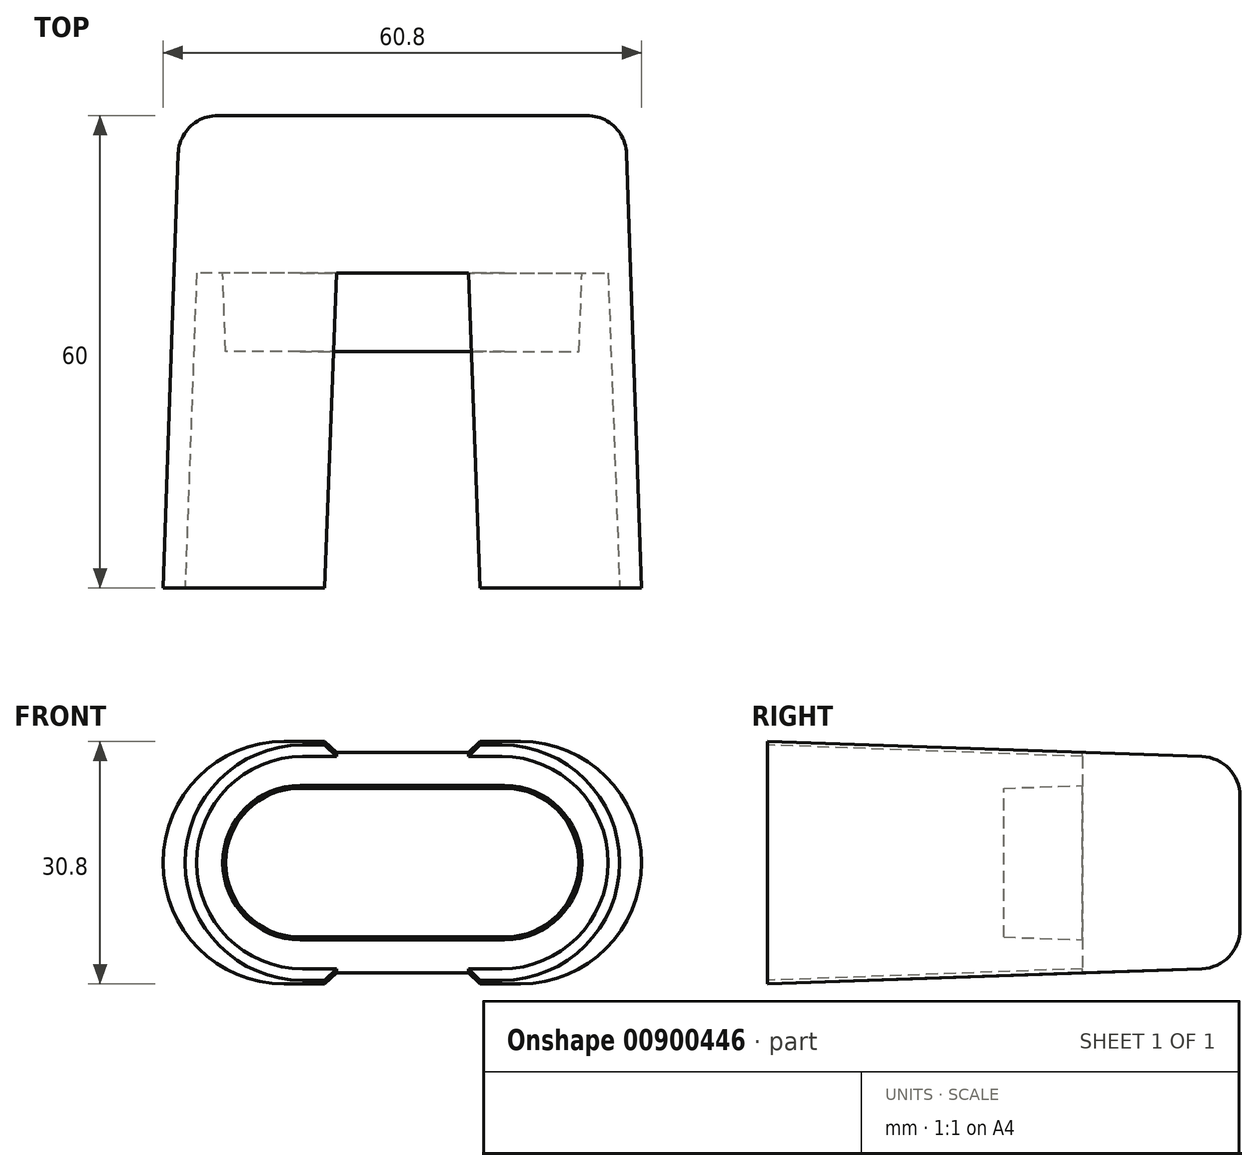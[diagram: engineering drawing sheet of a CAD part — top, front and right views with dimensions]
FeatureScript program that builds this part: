
annotation { "Feature Type Name" : "Feature", "Feature Type Description" : "" }
export const myFeature = defineFeature(function(context is Context, id is Id, definition is map)
    precondition{}
    {
        {
            var Q0;
            Q0=qCreatedBy(makeId("Front.planeOp"),FACE);
            var sketch = newSketch(context, id + "F0", { "sketchPlane" : qUnion([Q0])});
            skLineSegment(sketch, "E0", {"start": v(0, 0) * mm, "end": v(-28.3, 0) * mm, "construction": true});
            skLineSegment(sketch, "E1", {"start": v(0, 0) * mm, "end": v(0, 13.5) * mm, "construction": true});
            skLineSegment(sketch, "E2", {"start": v(-28.3, 0) * mm, "end": v(-28.3, 0) * mm});
            skLineSegment(sketch, "E3", {"start": v(-15, 13.3) * mm, "end": v(15, 13.3) * mm});
            skLineSegment(sketch, "E4", {"start": v(28.3, 0) * mm, "end": v(28.3, 0) * mm});
            skLineSegment(sketch, "E5", {"start": v(15, -13.3) * mm, "end": v(-15, -13.3) * mm});
            skPoint(sketch, "E6.visualSharp", {"position": v(-28.3, 13.3) * mm});
            skArc(sketch, "E6.filletArc", {"start": v(-15, 13.3) * mm, "mid": v(-24.4, 9.4) * mm, "end": v(-28.3, 0) * mm});
            skPoint(sketch, "E7.visualSharp", {"position": v(-28.3, -13.3) * mm});
            skArc(sketch, "E7.filletArc", {"start": v(-28.3, 0) * mm, "mid": v(-24.4, -9.4) * mm, "end": v(-15, -13.3) * mm});
            skPoint(sketch, "E8.visualSharp", {"position": v(28.3, -13.3) * mm});
            skArc(sketch, "E8.filletArc", {"start": v(15, -13.3) * mm, "mid": v(24.4, -9.4) * mm, "end": v(28.3, 0) * mm});
            skPoint(sketch, "E9.visualSharp", {"position": v(28.3, 13.3) * mm});
            skArc(sketch, "E9.filletArc", {"start": v(28.3, 0) * mm, "mid": v(24.4, 9.4) * mm, "end": v(15, 13.3) * mm});
            skSolve(sketch);
        }
        {
            var Q0;
            Q0=makeQuery(id+"F0.imprint","IMPRINT",FACE,{"disambiguationData":[TD([[makeQuery(id+"F0.imprint","IMPRINT",EDGE,{"derivedFrom":sQuery(id+"F0.wireOp",EDGE,"E3")}),-1.0]])]});
            extrude(context, id + "F1", {"entities" : qUnion([Q0]), "depth" : 60 * mm, "offsetDistance" : 25 * mm, "hasDraft" : true, "draftAngle" : 2 * degree});
        }
        {
            var Q0;
            Q0=qCreatedBy(makeId("Front.planeOp"),FACE);
            var sketch = newSketch(context, id + "F2", { "sketchPlane" : qUnion([Q0])});
            skLineSegment(sketch, "E10", {"start": v(0, 0) * mm, "end": v(-25.4, 0) * mm, "construction": true});
            skLineSegment(sketch, "E11", {"start": v(-25.4, 0) * mm, "end": v(-25.4, 0) * mm});
            skLineSegment(sketch, "E12", {"start": v(25.4, 0) * mm, "end": v(25.4, 0) * mm});
            skPoint(sketch, "E13.visualSharp", {"position": v(-25.4, 12.75) * mm});
            skArc(sketch, "E13.filletArc", {"start": v(-12.65, 12.75) * mm, "mid": v(-21.67, 9.02) * mm, "end": v(-25.4, 0) * mm});
            skPoint(sketch, "E14.visualSharp", {"position": v(-25.4, -12.75) * mm});
            skArc(sketch, "E14.filletArc", {"start": v(-25.4, 0) * mm, "mid": v(-21.67, -9.02) * mm, "end": v(-12.65, -12.75) * mm});
            skPoint(sketch, "E15.visualSharp", {"position": v(25.4, -12.75) * mm});
            skArc(sketch, "E15.filletArc", {"start": v(12.65, -12.75) * mm, "mid": v(21.67, -9.02) * mm, "end": v(25.4, 0) * mm});
            skPoint(sketch, "E16.visualSharp", {"position": v(25.4, 12.75) * mm});
            skArc(sketch, "E16.filletArc", {"start": v(25.4, 0) * mm, "mid": v(21.67, 9.02) * mm, "end": v(12.65, 12.75) * mm});
            skLineSegment(sketch, "E17", {"start": v(12.65, 12.75) * mm, "end": v(7.65, 12.75) * mm});
            skLineSegment(sketch, "E18", {"start": v(-12.65, 12.75) * mm, "end": v(-7.65, 12.75) * mm});
            skLineSegment(sketch, "E19", {"start": v(12.65, -12.75) * mm, "end": v(7.65, -12.75) * mm});
            skLineSegment(sketch, "E20", {"start": v(-12.65, -12.75) * mm, "end": v(-7.65, -12.75) * mm});
            skLineSegment(sketch, "E21", {"start": v(7.65, 12.75) * mm, "end": v(7.65, 18.8) * mm});
            skLineSegment(sketch, "E22", {"start": v(7.65, 18.8) * mm, "end": v(-7.65, 18.8) * mm});
            skLineSegment(sketch, "E23", {"start": v(-7.65, 12.75) * mm, "end": v(-7.65, 18.8) * mm});
            skLineSegment(sketch, "E24", {"start": v(7.65, -12.75) * mm, "end": v(7.65, -18.81) * mm});
            skLineSegment(sketch, "E25", {"start": v(7.65, -18.81) * mm, "end": v(-7.65, -18.81) * mm});
            skLineSegment(sketch, "E26", {"start": v(-7.65, -18.81) * mm, "end": v(-7.65, -12.75) * mm});
            skSolve(sketch);
        }
        {
            var Q0;
            Q0 = qSketchRegion(id + "F2", true);
            extrude(context, id + "F3", {"entities" : qUnion([Q0]), "operationType" : NewBodyOperationType.REMOVE, "depth" : 60 * mm, "offsetDistance" : 25 * mm, "hasDraft" : true, "draftAngle" : 2.1 * degree, "hasSecondDirection" : true, "secondDirectionOppositeDirection" : false, "secondDirectionDepth" : 20 * mm});
        }
        {
            var Q0;
            Q0=makeQuery(id+"F1.opExtrude","CAP_EDGE",EDGE,{"disambiguationData":[OSD([sQuery(id+"F0.wireOp",EDGE,"E6.filletArc"),sQuery(id+"F0.wireOp",EDGE,"E7.filletArc")])],"isStart":true});
            fillet(context, id + "F4", {"entities" : qUnion([Q0]), "radius" : 5 * mm, "tangentPropagation" : true, "allowEdgeOverflow" : false});
        }
        {
            var Q0;
            Q0=qCreatedBy(makeId("Front.planeOp"),FACE);
            var sketch = newSketch(context, id + "F5", { "sketchPlane" : qUnion([Q0])});
            skLineSegment(sketch, "E27", {"start": v(0, 0) * mm, "end": v(23.5, 0) * mm, "construction": true});
            skLineSegment(sketch, "E28", {"start": v(23.5, 0) * mm, "end": v(23.5, 0) * mm});
            skLineSegment(sketch, "E29", {"start": v(13, 10.5) * mm, "end": v(-13, 10.5) * mm});
            skLineSegment(sketch, "E30", {"start": v(-23.5, 0) * mm, "end": v(-23.5, 0) * mm});
            skLineSegment(sketch, "E31", {"start": v(-13, -10.5) * mm, "end": v(13, -10.5) * mm});
            skPoint(sketch, "E32.visualSharp", {"position": v(23.5, 10.5) * mm});
            skArc(sketch, "E32.filletArc", {"start": v(23.5, 0) * mm, "mid": v(20.42, 7.42) * mm, "end": v(13, 10.5) * mm});
            skPoint(sketch, "E33.visualSharp", {"position": v(23.5, -10.5) * mm});
            skArc(sketch, "E33.filletArc", {"start": v(13, -10.5) * mm, "mid": v(20.42, -7.42) * mm, "end": v(23.5, 0) * mm});
            skPoint(sketch, "E34.visualSharp", {"position": v(-23.5, -10.5) * mm});
            skArc(sketch, "E34.filletArc", {"start": v(-23.5, 0) * mm, "mid": v(-20.42, -7.42) * mm, "end": v(-13, -10.5) * mm});
            skPoint(sketch, "E35.visualSharp", {"position": v(-23.5, 10.5) * mm});
            skArc(sketch, "E35.filletArc", {"start": v(-13, 10.5) * mm, "mid": v(-20.42, 7.42) * mm, "end": v(-23.5, 0) * mm});
            skSolve(sketch);
        }
        {
            var Q0;
            Q0 = qSketchRegion(id + "F5", true);
            extrude(context, id + "F6", {"entities" : qUnion([Q0]), "operationType" : NewBodyOperationType.ADD, "depth" : 30 * mm, "offsetDistance" : 25 * mm, "hasDraft" : true, "draftAngle" : 2 * degree, "draftPullDirection" : true, "hasSecondDirection" : true, "secondDirectionOppositeDirection" : false, "secondDirectionDepth" : 5 * mm});
        }
    });
